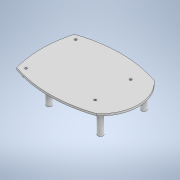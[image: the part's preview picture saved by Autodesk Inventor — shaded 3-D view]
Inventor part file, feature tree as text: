
AUTODESK INVENTOR PART (.ipt)
format: ipt  version: 2021 (Build 250183000, 183)  size: 359,424 bytes
history: native  units: mm
features: sketch x3, extrude x3, other x2, plane x1
ambient origin geometry x8: Origin, YZ Plane, XZ Plane, XY Plane, X Axis, Y Axis, Z Axis, Center Point
bodies: Volumenkörper1 (feature_tree)
feature tree (9):
  sketch  "Skizze4"  dims[d28=80.0mm d30=90.0mm]
  sketch  "Skizze3"  dims[d19=2.45mm d20=5.8mm]
  extrude  "Extrusion1"  Depth=5.8mm
  extrude  "Extrusion2"  Depth=90.0mm
  extrude  "Extrusion3"  Depth=3.0mm
  plane  "Arbeitsebene1"
  sketch  "Skizze6"  dims[d31=58.0mm d32=49.0mm d33=56.0mm d34=40.0mm d35=70.0mm d36=65.0mm d37=65.0mm d38=22.47mm d39=120.0mm d40=6.0mm d41=2.45mm d42=43.0mm d43=2.2mm d44=0.0mm d45=24.0mm d46=0.0mm d47=60.0deg d48=3.0mm d49=0.45mm d50=2.512875mm d51=0.243562mm d52=0.048713mm d53=60.0deg d54=3.0mm d55=0.45mm d56=2.512875mm d57=0.3897mm d58=6.0mm d59=5.0mm d60=0.0mm d62=0.0mm d71=60.0deg d72=3.0mm d73=0.45mm d74=2.512875mm d75=0.243563mm d76=0.048713mm d77=60.0deg d78=3.0mm d79=0.45mm d80=2.512875mm d81=0.3897mm d82=0.0mm]
  other  "Arbeitsachse1"
  other  "Arbeitsachse2"
